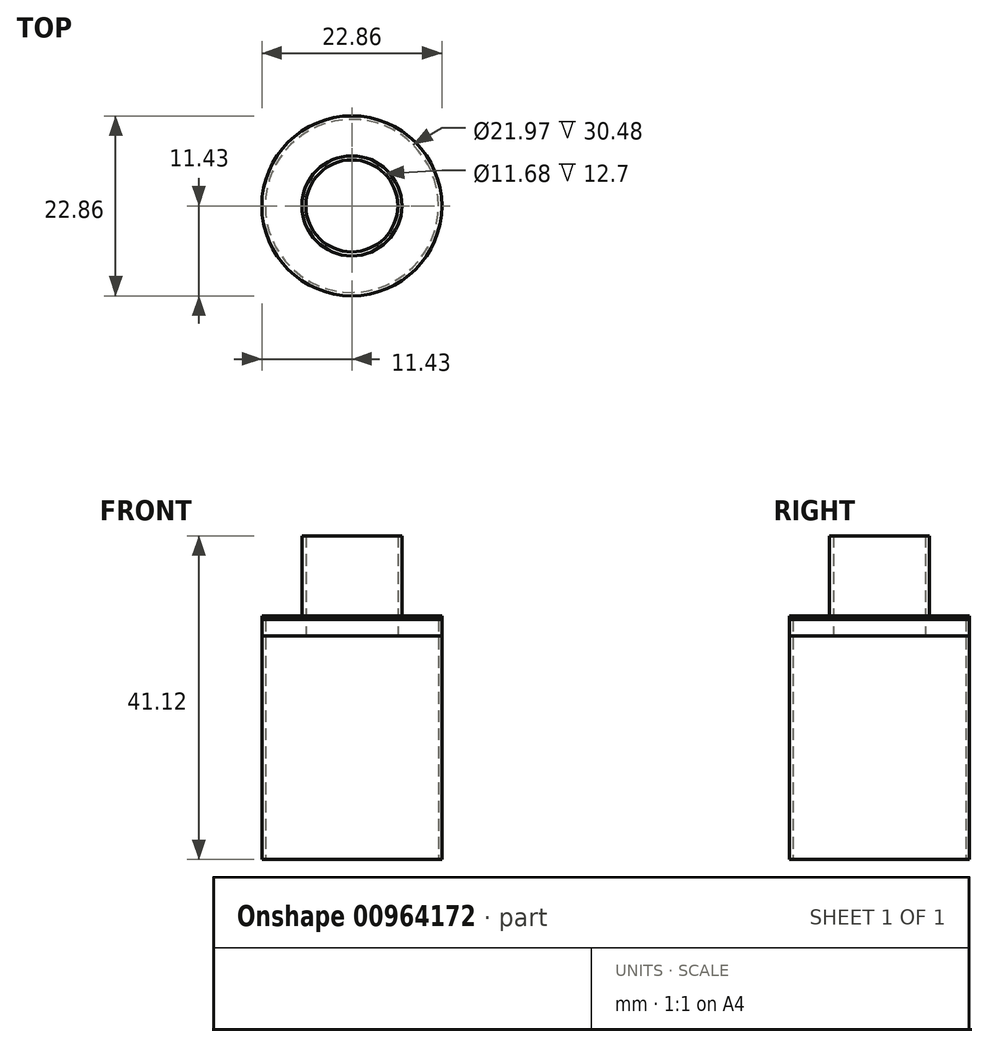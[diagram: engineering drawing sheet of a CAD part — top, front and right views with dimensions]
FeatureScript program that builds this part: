
annotation { "Feature Type Name" : "Feature", "Feature Type Description" : "" }
export const myFeature = defineFeature(function(context is Context, id is Id, definition is map)
    precondition{}
    {
        {
            var Q0;
            Q0=qCreatedBy(makeId("Top.planeOp"),FACE);
            var sketch = newSketch(context, id + "F0", { "sketchPlane" : qUnion([Q0])});
            skCircle(sketch, "E0", {"center": v(0, 0) * mm, "radius": 5.84 * mm});
            skCircle(sketch, "E1", {"center": v(0, 0) * mm, "radius": 6.35 * mm});
            skCircle(sketch, "E2", {"center": v(0, 0) * mm, "radius": 10.99 * mm});
            skCircle(sketch, "E3", {"center": v(0, 0) * mm, "radius": 11.43 * mm});
            skSolve(sketch);
        }
        {
            var Q0;
            Q0=makeQuery(id+"F0.imprint","IMPRINT",FACE,{"disambiguationData":[TD([[makeQuery(id+"F0.imprint","IMPRINT",EDGE,{"derivedFrom":sQuery(id+"F0.wireOp",EDGE,"E0")}),-1.0]])]});
            extrude(context, id + "F1", {"entities" : qUnion([Q0]), "depth" : 12.7 * mm, "offsetDistance" : 25.4 * mm});
        }
        {
            var Q0;
            Q0=makeQuery(id+"F0.imprint","IMPRINT",FACE,{"disambiguationData":[TD([[makeQuery(id+"F0.imprint","IMPRINT",EDGE,{"derivedFrom":sQuery(id+"F0.wireOp",EDGE,"E1")}),-1.0]])]});
            var Q1;
            Q1=makeQuery(id+"F0.imprint","IMPRINT",FACE,{"disambiguationData":[TD([[makeQuery(id+"F0.imprint","IMPRINT",EDGE,{"derivedFrom":sQuery(id+"F0.wireOp",EDGE,"E2")}),-1.0]])]});
            extrude(context, id + "F2", {"entities" : qUnion([Q0, Q1]), "operationType" : NewBodyOperationType.ADD, "depth" : 2.54 * mm, "offsetDistance" : 25.4 * mm});
        }
        {
            var Q0;
            Q0=makeQuery(id+"F0.imprint","IMPRINT",FACE,{"disambiguationData":[TD([[makeQuery(id+"F0.imprint","IMPRINT",EDGE,{"derivedFrom":sQuery(id+"F0.wireOp",EDGE,"E2")}),-1.0]])]});
            extrude(context, id + "F3", {"entities" : qUnion([Q0]), "depth" : 30.48 * mm, "offsetDistance" : 25.4 * mm});
        }
        {
            var Q0;
            Q0=makeQuery(id+"F1.opExtrude","SWEPT_BODY",BODY,{"disambiguationData":[OSD([sQuery(id+"F0.wireOp",EDGE,"E0"),sQuery(id+"F0.wireOp",EDGE,"E1")])]});
            transform(context, id + "F4", {"entities" : qUnion([Q0]), "transformType" : TransformType.TRANSLATION_3D, "dx" : 0 * mm, "dy" : 0 * mm, "dz" : 28.42 * mm, "makeCopy" : false});
        }
    });
